# Revit family: 50528_jumping jet rainbow
name_source: partatom
category: Körper
revit_build: Autodesk Revit 2015 (Build: 20140606_1530(x64)
units: mm (PartAtom-declared; Revit-internal decimal feet)

## types (1)
- jumping Jet Rainbow Flash II / DMX/02
    Beschreibung = controllable Nozzles
    Dimensions  LxWxH = 530x390x660 mm
    Environmental condition , submersible application = water temperature: min 4 °C to max. 35 °C
    Environmental condition, dry application = Ambient temperature: max.  30 ° C with natural convection, max. 40 ° C ith forced convection, no direct sun exposure permitted
    Hersteller = OASE GmbH Post Box 2069, 48469 Hörstel , Germany +49 5454 80-0
    Homepage = http://www.oase-livingwater.com
    Jet diameter = 18 mm
    Light type = LED RGB multiple spotlights
    Material = Plastic / stainless steel 1.4301 ( AISI 304 )
    Max. pressure = 0.5 bar
    Max. water depth ( wet installation) = 250 mm
    Max.Water parabola laminar = 7 m
    Max.Water parabola laminar with light = 6 m
    Modell = jumping Jet Rainbow Flash II / DMX/02
    Name = jumping Jet Rainbow Flash II / DMX/02
    Number of DMX channels = 8 channels, start number 1
    Outflow side connection = Hose connection 2 "
    Pressure side connection = Hose connection 1 1/2"
    RDM-DMX connection = 1 box
    Rated voltage, mechanical / illumination = 12 V/AC
    Total  consumption = 20 W
    Vertical pivoting range = 45-90 °
    Weight = 50 kg
    oder no. = 50528

## geometry (parser evidence)
native form markers: Blend x6
no freeform markers — native parametric forms only
